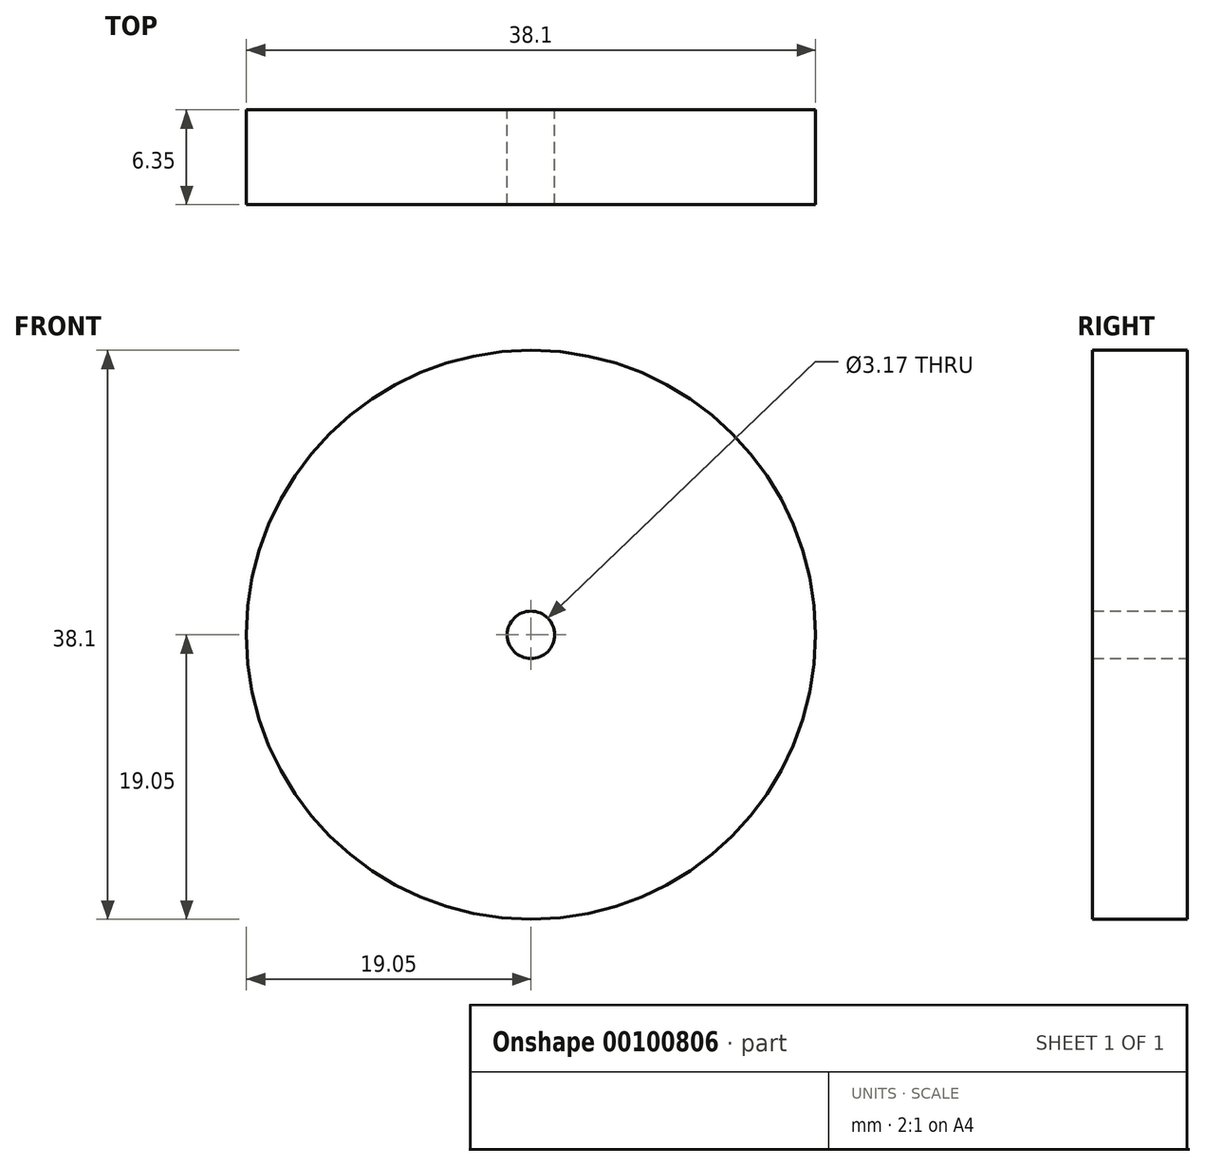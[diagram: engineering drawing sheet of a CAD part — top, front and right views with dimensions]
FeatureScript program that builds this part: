
annotation { "Feature Type Name" : "Feature", "Feature Type Description" : "" }
export const myFeature = defineFeature(function(context is Context, id is Id, definition is map)
    precondition{}
    {
        {
            var Q0;
            Q0=qCreatedBy(makeId("Front.planeOp"),FACE);
            var sketch = newSketch(context, id + "F0", { "sketchPlane" : qUnion([Q0])});
            skCircle(sketch, "E0", {"center": v(0, 0) * mm, "radius": 19.05 * mm});
            skCircle(sketch, "E1", {"center": v(0, 0) * mm, "radius": 1.59 * mm});
            skSolve(sketch);
        }
        {
            var Q0;
            Q0 = qSketchRegion(id + "F0", true);
            extrude(context, id + "F1", {"entities" : qUnion([Q0]), "depth" : 6.35 * mm});
        }
    });
